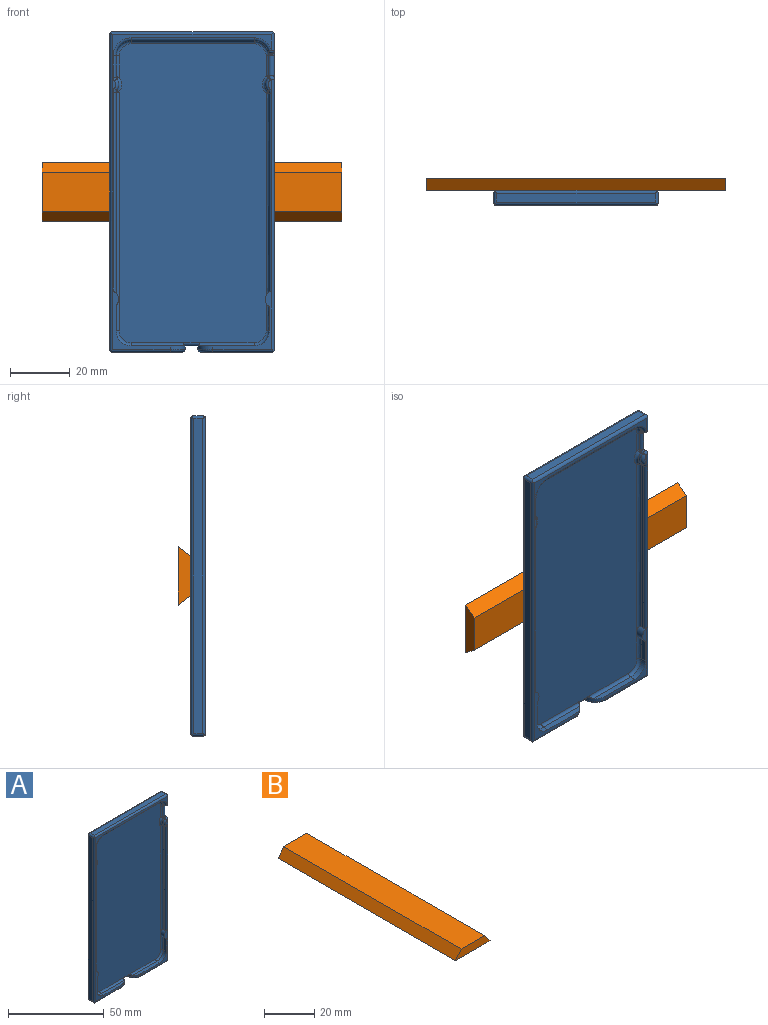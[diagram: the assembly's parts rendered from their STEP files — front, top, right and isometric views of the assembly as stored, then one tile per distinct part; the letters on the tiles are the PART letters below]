
ASSEMBLY  parts=2 mates=1
PART A: 89 faces, bbox 55.4x6x107 mm
  f0: cylinder r=1mm len=1.95mm, axis (0,-1,0), area 1.8mm2, adj f1,f18,f23,f82
  f1: bspline ~1.95x1.27mm, area 2.3mm2, adj f0,f18,f23,f37,f83
  f2: plane 19.44x19.44mm, normal (0,-1,0), area 43.7mm2, adj f22,f28,f29,f32,f45,f71,f88
  f3: plane 3.74x0.96mm, normal (0,-1,0), area 2.4mm2, adj f65,f67,f68,f88
  f4: cylinder r=1mm len=79.63mm, axis (0,0,-1), area 120.3mm2, adj f9,f10,f26,f34,f46,f60
  f5: cylinder r=3mm len=4.37mm, axis (0,-1,0), area 4.9mm2, adj f62,f63,f66,f67
  f6: plane 104.83x52.84mm, normal (0,-1,0), area 126.7mm2, adj f16,f26,f27,f31,f41,f46,f48,f49
  f7: plane 66.24x1mm, normal (-1,0,0), area 66.2mm2, adj f8,f45,f66,f69
  f8: cylinder r=1mm len=67.47mm, axis (0,0,1), area 105mm2, adj f7,f10,f45,f64
  f9: plane 66.97x1mm, normal (1,0,0), area 67mm2, adj f4,f46,f54,f59
  f10: plane 99.71x49.05mm, normal (0,-1,0), area 4868.1mm2, adj f4,f8,f11,f12,f14,f33,f34,f35
  f11: cylinder r=1mm len=9.32mm, axis (0,0,1), area 13.7mm2, adj f10,f22,f38,f45
  f12: cylinder r=1mm len=6.67mm, axis (0,0,1), area 6.8mm2, adj f10,f37,f61,f84
  f13: plane 7.09x1mm, normal (1,0,0), area 7.1mm2, adj f14,f25,f51,f53
  f14: cylinder r=1mm len=7.09mm, axis (0,0,-1), area 11.1mm2, adj f10,f13,f35,f56
  f15: plane 22.99x3mm, normal (0,0,-1), area 66mm2, adj f74,f75,f76,f77
  f16: plane 17.03x2mm, normal (0,0,1), area 31.7mm2, adj f6,f27,f31,f33
  f17: plane 23.31x3mm, normal (0,0,-1), area 66.9mm2, adj f70,f71,f72,f73
  f18: plane 104.96x3.12mm, normal (1,0,0), area 296mm2, adj f0,f1,f43,f70,f80,f81,f83,f84
  f19: plane 52.84x3mm, normal (0,0,1), area 158.5mm2, adj f40,f41,f42,f43
  f20: plane 104.83x3mm, normal (-1,0,0), area 314.5mm2, adj f40,f74,f78,f79
  f21: plane 104.83x52.84mm, normal (0,1,0), area 5534.8mm2, adj f30,f31,f32,f42,f72,f75,f78,f80
  f22: plane 8.09x2mm, normal (-1,0,0), area 16.2mm2, adj f2,f11,f29,f45
  f23: cylinder r=5mm len=4.76mm, axis (0,-1,0), area 6.3mm2, adj f0,f1,f24,f37,f48
  f24: plane 41.05x1mm, normal (0,0,-1), area 41mm2, adj f23,f25,f36,f49
  f25: cylinder r=5mm len=5mm, axis (0,-1,0), area 7.9mm2, adj f13,f24,f35,f50
  f26: plane 8.41x2mm, normal (1,0,0), area 16.8mm2, adj f4,f6,f27,f46
  f27: cylinder r=5mm len=5mm, axis (0,-1,0), area 15.7mm2, adj f6,f16,f26,f34
  f28: plane 17.73x2mm, normal (0,0,1), area 33mm2, adj f2,f29,f32,f39
  f29: cylinder r=5mm len=5mm, axis (0,-1,0), area 15.7mm2, adj f2,f22,f28,f38
  f30: plane 4.49x1mm, normal (0,0,-1), area 4.4mm2, adj f21,f31,f32,f47
  f31: cylinder r=5mm len=5mm, axis (0,0,1), area 9.6mm2, adj f6,f16,f21,f30,f33,f47,f77
  f32: cylinder r=5mm len=5mm, axis (0,0,-1), area 9.6mm2, adj f2,f21,f28,f30,f39,f47,f73
  f33: cylinder r=1mm len=17.61mm, axis (1,0,0), area 27.2mm2, adj f10,f16,f31,f34
  f34: torus R=4mm, axis (0,-1,0), area 11.4mm2, adj f4,f10,f27,f33
  f35: torus R=4mm, axis (0,-1,0), area 11.4mm2, adj f10,f14,f25,f36
  f36: cylinder r=1mm len=41.05mm, axis (-1,0,0), area 64.5mm2, adj f10,f24,f35,f37
  f37: torus R=4mm, axis (0,-1,0), area 10.9mm2, adj f1,f10,f12,f23,f36,f83
  f38: torus R=4mm, axis (0,-1,0), area 11.4mm2, adj f10,f11,f29,f39
  f39: cylinder r=1mm len=18.31mm, axis (1,0,0), area 28.3mm2, adj f10,f28,f32,f38
  f40: cylinder r=1mm len=4.41mm, axis (0,-1,0), area 5.8mm2, adj f19,f20,f41,f42,f78,f79
  f41: cylinder r=1mm len=54.25mm, axis (1,0,0), area 84.1mm2, adj f6,f19,f40,f43,f79,f81
  f42: cylinder r=1mm len=54.25mm, axis (-1,0,0), area 84.1mm2, adj f19,f21,f40,f43,f78,f80
  f43: cylinder r=1mm len=4.41mm, axis (0,1,0), area 5.8mm2, adj f18,f19,f41,f42,f80,f81
  f44: cylinder r=3mm len=3.75mm, axis (0,-1,0), area 4mm2, adj f53,f55,f58,f59
  f45: cylinder r=3mm len=5.31mm, axis (0,-1,0), area 16.8mm2, adj f2,f7,f8,f10,f11,f22,f69,f88
  f46: cylinder r=3mm len=4.9mm, axis (0,-1,0), area 14mm2, adj f4,f6,f9,f26,f54
  f47: cylinder r=1mm len=5.12mm, axis (1,0,0), area 7.5mm2, adj f10,f30,f31,f32
  f48: torus R=6mm, axis (0,-1,0), area 10.6mm2, adj f6,f23,f49,f82
  f49: cylinder r=1mm len=41.05mm, axis (1,0,0), area 64.5mm2, adj f6,f24,f48,f50
  f50: torus R=6mm, axis (0,-1,0), area 13.2mm2, adj f6,f25,f49,f51
  f51: cylinder r=1mm len=7.09mm, axis (0,0,1), area 11.1mm2, adj f6,f13,f50,f52
  f52: torus R=2mm, axis (0,-1,0), area 1.4mm2, adj f6,f51,f53,f55
  f53: cylinder r=1mm len=1mm, axis (0,-1,0), area 0.7mm2, adj f13,f44,f52,f56
  f54: cylinder r=1mm len=66.97mm, axis (0,0,1), area 104.7mm2, adj f6,f9,f46,f57
  f55: torus R=2mm, axis (0,-1,0), area 5.6mm2, adj f6,f44,f52,f57
  f56: sphere r=1mm, area 0.9mm2, adj f14,f53,f58
  f57: torus R=2mm, axis (0,-1,0), area 1.4mm2, adj f6,f54,f55,f59
  f58: torus R=4mm, axis (0,-1,0), area 7.1mm2, adj f10,f44,f56,f60
  f59: cylinder r=1mm len=1mm, axis (0,-1,0), area 0.7mm2, adj f9,f44,f57,f60
  f60: sphere r=1mm, area 0.9mm2, adj f4,f58,f59
  f61: sphere r=1mm, area 0.6mm2, adj f12,f62,f63,f85
  f62: torus R=4mm, axis (0,-1,0), area 8.6mm2, adj f5,f10,f61,f64
  f63: cylinder r=1mm len=1mm, axis (0,-1,0), area 0.3mm2, adj f5,f61,f65,f86
  f64: sphere r=1mm, area 1mm2, adj f8,f62,f66
  f65: torus R=2mm, axis (0,-1,0), area 0.6mm2, adj f3,f63,f67,f87
  f66: cylinder r=1mm len=1mm, axis (0,-1,0), area 0.8mm2, adj f5,f7,f64,f68
  f67: torus R=2mm, axis (0,-1,0), area 6.8mm2, adj f3,f5,f65,f68
  f68: torus R=2mm, axis (0,-1,0), area 1.7mm2, adj f3,f66,f67,f69,f88
  f69: cylinder r=1mm len=66.24mm, axis (0,0,-1), area 94mm2, adj f7,f45,f68,f88
  f70: cylinder r=1mm len=4.41mm, axis (0,-1,0), area 5.8mm2, adj f17,f18,f71,f72,f80,f88
  f71: cylinder r=1mm len=20.14mm, axis (-1,0,0), area 31.1mm2, adj f2,f17,f70,f73,f88
  f72: cylinder r=1mm len=25.14mm, axis (1,0,0), area 38.1mm2, adj f17,f21,f70,f73,f80
  f73: torus R=4mm, axis (0,0,-1), area 10.6mm2, adj f17,f32,f71,f72
  f74: cylinder r=1mm len=4.41mm, axis (0,1,0), area 5.8mm2, adj f15,f20,f75,f76,f78,f79
  f75: cylinder r=1mm len=24.82mm, axis (1,0,0), area 37.6mm2, adj f15,f21,f74,f77,f78
  f76: cylinder r=1mm len=19.82mm, axis (-1,0,0), area 30.6mm2, adj f6,f15,f74,f77,f79
  f77: torus R=4mm, axis (0,0,-1), area 10.6mm2, adj f15,f31,f75,f76
  f78: cylinder r=1mm len=106.25mm, axis (0,0,-1), area 165.8mm2, adj f20,f21,f40,f42,f74,f75
  f79: cylinder r=1mm len=106.25mm, axis (0,0,1), area 165.8mm2, adj f6,f20,f40,f41,f74,f76
  f80: cylinder r=1mm len=106.25mm, axis (0,0,1), area 165.8mm2, adj f18,f21,f42,f43,f70,f72
  f81: cylinder r=1mm len=5.89mm, axis (0,0,-1), area 8.7mm2, adj f6,f18,f41,f43,f82
  f82: sphere r=1mm, area 2.4mm2, adj f0,f48,f81
  f83: bspline ~3.96x1.92mm, area 1.8mm2, adj f1,f18,f37,f84
  f84: cylinder r=1mm len=6.67mm, axis (0,0,1), area 17.3mm2, adj f12,f18,f83,f85
  f85: torus R=1.04mm, axis (-1,0,0), area 1.3mm2, adj f18,f61,f84,f86
  f86: cylinder r=1mm len=1.85mm, axis (0,-1,0), area 2.6mm2, adj f18,f63,f85,f87
  f87: sphere r=1mm, area 2.6mm2, adj f65,f86,f88
  f88: cylinder r=1mm len=90.79mm, axis (0,0,-1), area 132.3mm2, adj f2,f3,f18,f45,f68,f69,f70,f71
PART B: 6 faces, bbox 19.5x100x4.1 mm
  f0: plane 100x4.1mm, normal (-0.79,0,0.62), area 520.3mm2, adj f1,f3,f4,f5
  f1: plane 100x19.5mm, normal (0,0,-1), area 1950mm2, adj f0,f2,f4,f5
  f2: plane 100x4.1mm, normal (0.79,0,0.62), area 520.3mm2, adj f1,f3,f4,f5
  f3: plane 100x13.09mm, normal (0,0,1), area 1309.3mm2, adj f0,f2,f4,f5
  f4: plane 19.5x4.1mm, normal (0,-1,0), area 66.8mm2, adj f0,f1,f2,f3
  f5: plane 19.5x4.1mm, normal (0,1,0), area 66.8mm2, adj f0,f1,f2,f3
PLACE A at identity
PLACE B rot(axis=(0.58,0.58,-0.58),120deg) t=(50,2.05,0.04)mm
MATE fastened B.f3 <-> A.f21  axis (0,-1,0) through (0,0,0.04)mm
